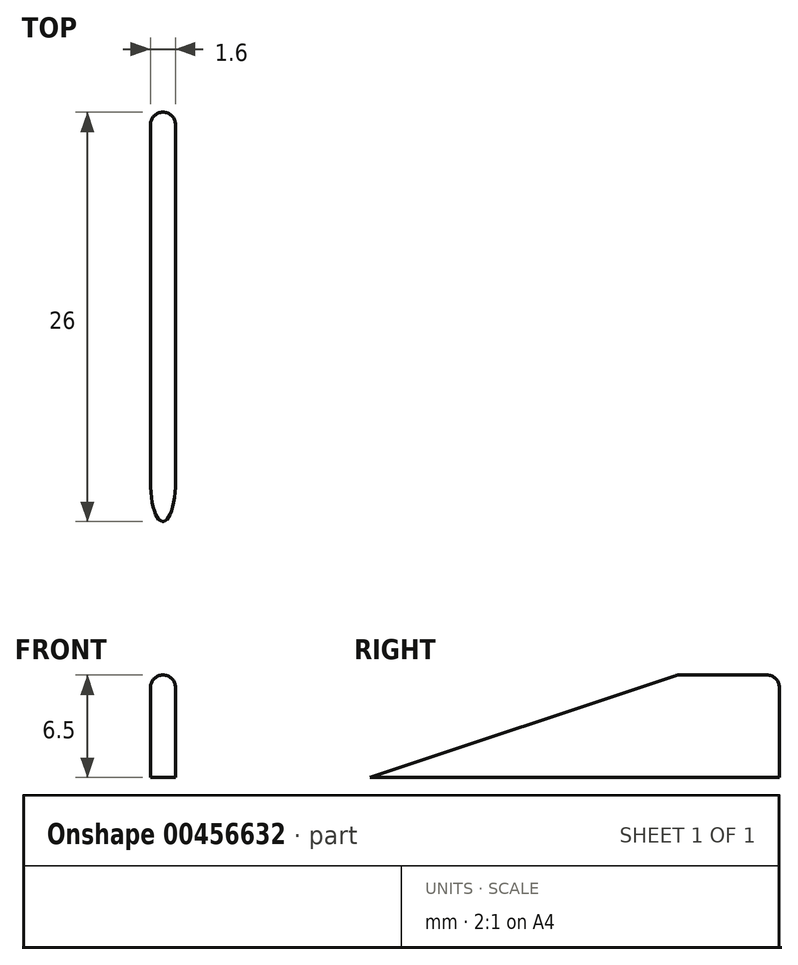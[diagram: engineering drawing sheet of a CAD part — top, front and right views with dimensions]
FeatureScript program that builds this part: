
annotation { "Feature Type Name" : "Feature", "Feature Type Description" : "" }
export const myFeature = defineFeature(function(context is Context, id is Id, definition is map)
    precondition{}
    {
        {
            var Q0;
            Q0=qCreatedBy(makeId("Right.planeOp"),FACE);
            var sketch = newSketch(context, id + "F0", { "sketchPlane" : qUnion([Q0])});
            skLineSegment(sketch, "E0", {"start": v(0, 0) * mm, "end": v(19.5, 6.5) * mm});
            skLineSegment(sketch, "E1", {"start": v(19.5, 6.5) * mm, "end": v(26, 6.5) * mm});
            skLineSegment(sketch, "E2", {"start": v(26, 6.5) * mm, "end": v(26, 0) * mm});
            skLineSegment(sketch, "E3", {"start": v(26, 0) * mm, "end": v(0, 0) * mm});
            skSolve(sketch);
        }
        {
            var Q0;
            Q0=makeQuery(id+"F0.imprint","IMPRINT",FACE,{"disambiguationData":[TD([[makeQuery(id+"F0.imprint","IMPRINT",EDGE,{"derivedFrom":sQuery(id+"F0.wireOp",EDGE,"E0")}),-1.0]])]});
            extrude(context, id + "F1", {"entities" : qUnion([Q0]), "endBound" : BoundingType.SYMMETRIC, "depth" : 1.6 * mm});
        }
        {
            var Q0;
            Q0=makeQuery(id+"F1.opExtrude","CAP_EDGE",EDGE,{"disambiguationData":[OSD([sQuery(id+"F0.wireOp",EDGE,"E1")])],"isStart":false});
            var Q1;
            Q1=makeQuery(id+"F1.opExtrude","CAP_EDGE",EDGE,{"disambiguationData":[OSD([sQuery(id+"F0.wireOp",EDGE,"E0")])],"isStart":false});
            var Q2;
            Q2=makeQuery(id+"F1.opExtrude","CAP_EDGE",EDGE,{"disambiguationData":[OSD([sQuery(id+"F0.wireOp",EDGE,"E1")])],"isStart":true});
            var Q3;
            Q3=makeQuery(id+"F1.opExtrude","CAP_EDGE",EDGE,{"disambiguationData":[OSD([sQuery(id+"F0.wireOp",EDGE,"E0")])],"isStart":true});
            var Q4;
            Q4=makeQuery(id+"F1.opExtrude","SWEPT_EDGE",EDGE,{"disambiguationData":[OSD([sQuery(id+"F0.wireOp",EDGE,"E0"),sQuery(id+"F0.wireOp",EDGE,"E1")])]});
            var Q5;
            Q5=makeQuery(id+"F1.opExtrude","SWEPT_EDGE",EDGE,{"disambiguationData":[OSD([sQuery(id+"F0.wireOp",EDGE,"E1"),sQuery(id+"F0.wireOp",EDGE,"E2")])]});
            var Q6;
            Q6=makeQuery(id+"F1.opExtrude","CAP_EDGE",EDGE,{"disambiguationData":[OSD([sQuery(id+"F0.wireOp",EDGE,"E2")])],"isStart":false});
            var Q7;
            Q7=makeQuery(id+"F1.opExtrude","CAP_EDGE",EDGE,{"disambiguationData":[OSD([sQuery(id+"F0.wireOp",EDGE,"E2")])],"isStart":true});
            fillet(context, id + "F2", {"entities" : qUnion([Q0, Q1, Q2, Q3, Q4, Q5, Q6, Q7]), "radius" : .8 * mm, "tangentPropagation" : true, "allowEdgeOverflow" : false});
        }
    });
